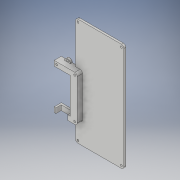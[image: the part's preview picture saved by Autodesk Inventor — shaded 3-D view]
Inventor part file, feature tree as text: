
AUTODESK INVENTOR PART (.ipt)
format: ipt  version: 2019 (Build 230136000, 136)  size: 195,584 bytes
history: native  units: in
note: dims shown in document units (in); Inventor stores cm internally (conversion verified against a paired STEP export)
features: sketch x5, hole x3, extrude x2, other x1
ambient origin geometry x8: Origin, YZ Plane, XZ Plane, XY Plane, X Axis, Y Axis, Z Axis, Center Point
bodies: Solid1 (feature_tree)
feature tree (11):
  other  "PhoneCover"
  extrude  "Phone Cover"  Depth=2.13in
  hole  "Phone Holes"  [1 undecoded]
  extrude  "Scanner Wall"  Depth=0.125in
  hole  "Scanner Holes"  [1 undecoded]
  hole  "Hole3"  [1 undecoded]
  sketch  "Sketch1"  dims[d0=2.43in d1=2.13in]
  sketch  "Sketch2"  dims[d4=1.0in d5=0.1in d6=0.0in]
  sketch  "Sketch3"  dims[d7=0.125in d8=0.125in]
  sketch  "Sketch4"  dims[d9=0.125in d10=0.125in]
  sketch  "Sketch5"  dims[d11=0.1in d12=0.75in d13=0.375in d14=0.25in d15=0.5635in d16=1.0in d17=0.8108in d22=0.81in d23=0.25in d24=0.25in d25=0.09in d26=0.125in d27=0.26in d28=0.0in d29=0.125in d30=0.125in d32=0.125in d33=0.35in d34=0.1in d35=0.75in d36=0.375in d37=0.25in d38=0.5635in d39=0.18in d40=0.8108in d41=0.125in d42=5.4in d43=0.125in d44=0.125in d45=0.125in d46=0.125in d48=0.125in d49=0.125in d50=0.125in d51=0.125in d52=0.3in d53=0.3in d54=0.06in d55=0.1in d56=0.75in d57=0.375in d58=0.25in d59=0.5635in d60=0.35in d61=0.8108in]
note: 3 required parameter values undecoded (feature->parameter linkage not recoverable at this tier; creation-order binding heuristic only, values carry confidence <= 0.55)
